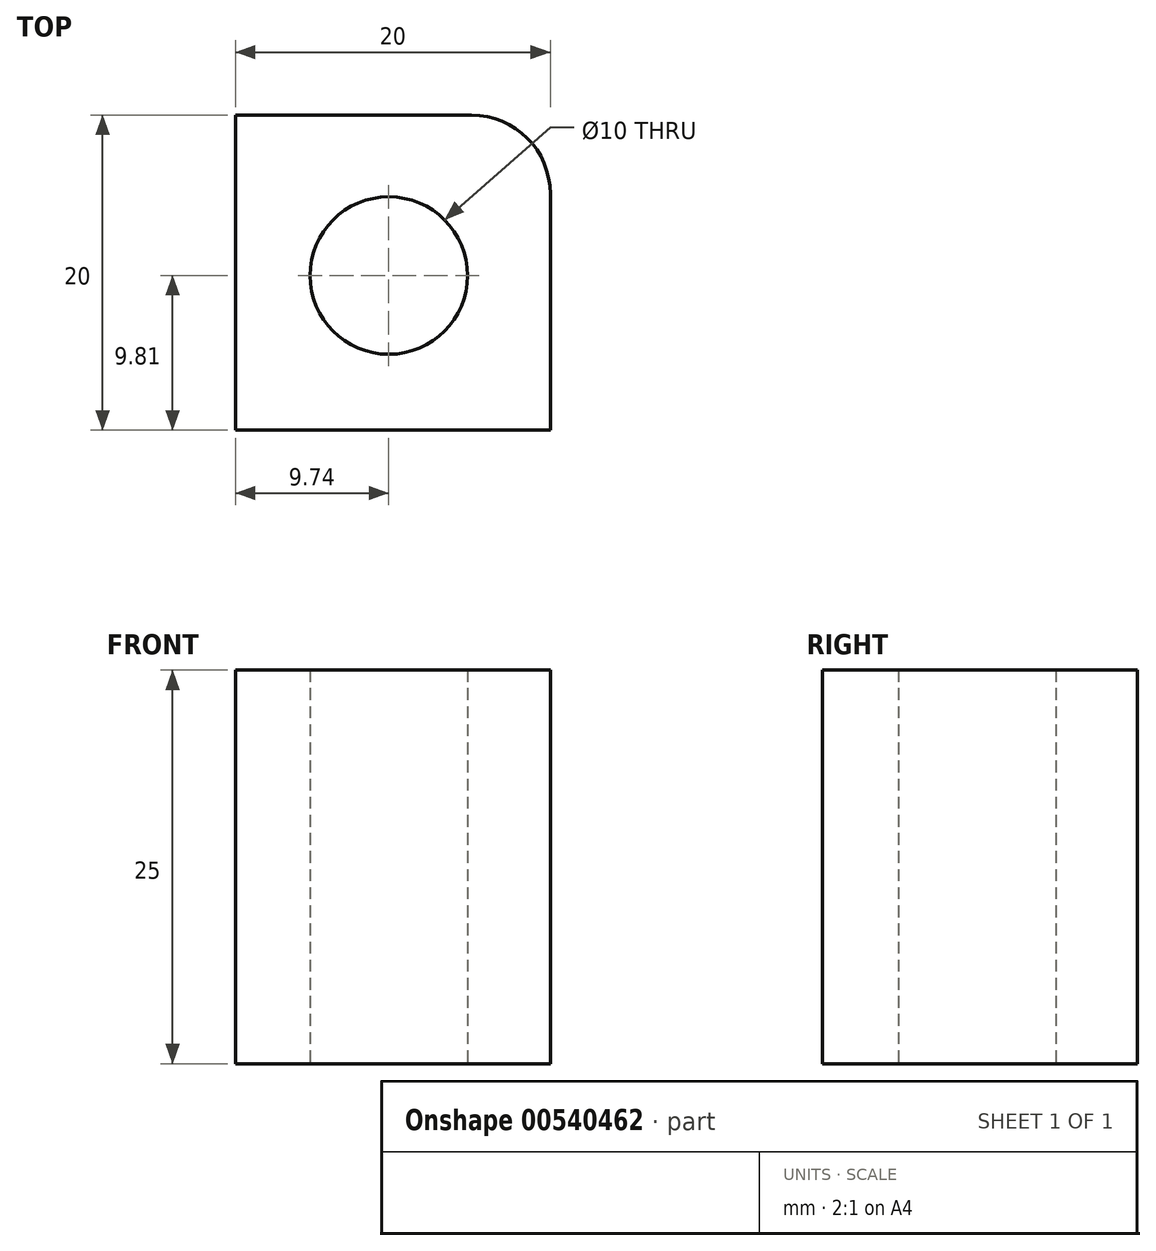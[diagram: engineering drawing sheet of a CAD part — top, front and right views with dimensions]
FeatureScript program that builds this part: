
annotation { "Feature Type Name" : "Feature", "Feature Type Description" : "" }
export const myFeature = defineFeature(function(context is Context, id is Id, definition is map)
    precondition{}
    {
        {
            var Q0;
            Q0=qCreatedBy(makeId("Top.planeOp"),FACE);
            var sketch = newSketch(context, id + "F0", { "sketchPlane" : qUnion([Q0])});
            skLineSegment(sketch, "E0.bottom", {"start": v(-9.74, 10.19) * mm, "end": v(5.26, 10.19) * mm});
            skLineSegment(sketch, "E0.top", {"start": v(-9.74, -9.81) * mm, "end": v(10.26, -9.81) * mm});
            skLineSegment(sketch, "E0.left", {"start": v(-9.74, 10.19) * mm, "end": v(-9.74, -9.81) * mm});
            skLineSegment(sketch, "E0.right", {"start": v(10.26, 5.19) * mm, "end": v(10.26, -9.81) * mm});
            skPoint(sketch, "E1.visualSharp", {"position": v(10.26, 10.19) * mm});
            skArc(sketch, "E1.filletArc", {"start": v(10.26, 5.19) * mm, "mid": v(8.8, 8.72) * mm, "end": v(5.26, 10.19) * mm});
            skCircle(sketch, "E2", {"center": v(0, 0) * mm, "radius": 5 * mm});
            skSolve(sketch);
        }
        {
            var Q0;
            Q0 = qSketchRegion(id + "F0", true);
            extrude(context, id + "F1", {"entities" : qUnion([Q0]), "depth" : 25 * mm, "offsetDistance" : 25 * mm});
        }
    });
